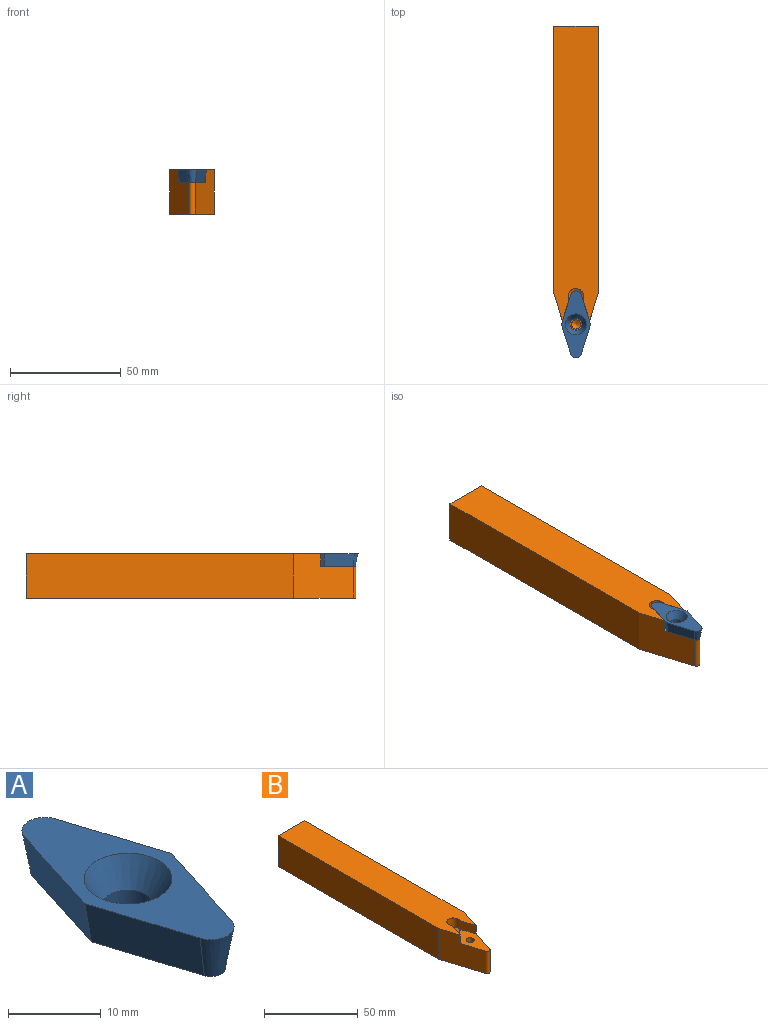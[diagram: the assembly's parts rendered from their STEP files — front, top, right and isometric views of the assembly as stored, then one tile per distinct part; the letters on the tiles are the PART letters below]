
ASSEMBLY  parts=2 mates=1
PART A: 10 faces, bbox 13.2x30.3x5.6 mm
  f0: plane 13.42x5.56mm, normal (-0.94,0.3,-0.17), area 78.5mm2, adj f1,f5,f6,f7
  f1: cone r=2.5mm half-angle=9.8deg, axis (0,0,1), area 28.8mm2, adj f0,f2,f6,f7
  f2: plane 13.42x5.56mm, normal (0.94,0.3,-0.17), area 78.5mm2, adj f1,f3,f6,f7
  f3: plane 13.42x5.56mm, normal (0.94,-0.3,-0.17), area 78.5mm2, adj f2,f4,f6,f7
  f4: cone r=2.5mm half-angle=9.8deg, axis (0,0,1), area 28.8mm2, adj f3,f5,f6,f7
  f5: plane 13.42x5.56mm, normal (-0.94,-0.3,-0.17), area 78.5mm2, adj f0,f4,f6,f7
  f6: plane 28.42x11.22mm, normal (0,0,-1), area 166.8mm2, adj f0,f1,f2,f3,f4,f5,f8
  f7: plane 30.34x13.23mm, normal (0,0,1), area 182.9mm2, adj f0,f1,f2,f3,f4,f5,f9
  f8: cylinder r=2.75mm len=5.5mm, axis (0,0,-1), area 36.2mm2, adj f6,f9
  f9: cone r=4.75mm half-angle=30deg, axis (0,0,1), area 94.2mm2, adj f7,f8
PART B: 15 faces, bbox 20x149x20 mm
  f0: plane 27.06x20mm, normal (-0.95,-0.3,0), area 481.5mm2, adj f1,f4,f5,f7,f10,f12
  f1: cylinder r=1.54mm len=14.44mm, axis (0,0,-1), area 56.3mm2, adj f0,f2,f7,f10
  f2: plane 27.06x20mm, normal (0.95,-0.3,0), area 481.5mm2, adj f1,f3,f4,f7,f10,f11
  f3: plane 120.91x20mm, normal (1,0,0), area 2418.1mm2, adj f2,f4,f6,f7
  f4: plane 133.24x20mm, normal (0,0,1), area 2499.2mm2, adj f0,f2,f3,f5,f6,f9,f11,f12
  f5: plane 120.91x20mm, normal (-1,0,0), area 2418.1mm2, adj f0,f4,f6,f7
  f6: plane 20x20mm, normal (0,1,0), area 400mm2, adj f3,f4,f5,f7
  f7: plane 149.04x20mm, normal (0,0,-1), area 2730.8mm2, adj f0,f1,f2,f3,f5,f6
  f8: cone r=0mm half-angle=59deg, axis (0,0,1), area 44.9mm2, adj f9
  f9: cylinder r=3.5mm len=7mm, axis (0,0,1), area 89.1mm2, adj f4,f8,f10,f11,f12
  f10: plane 25.29x12.23mm, normal (0,0,1), area 179.2mm2, adj f0,f1,f2,f9,f11,f12,f14
  f11: plane 9.49x5.56mm, normal (-0.95,-0.3,0), area 55.3mm2, adj f2,f4,f9,f10
  f12: plane 9.49x5.56mm, normal (0.95,-0.3,0), area 55.3mm2, adj f0,f4,f9,f10
  f13: cone r=0mm half-angle=59deg, axis (0,0,1), area 16.2mm2, adj f14
  f14: cylinder r=2.1mm len=10mm, axis (0,0,1), area 131.9mm2, adj f10,f13
PLACE A at identity
PLACE B at identity
MATE fastened A.f8 <-> B.f13  axis (0,0,-1) through (-60,-20.98,0)mm
